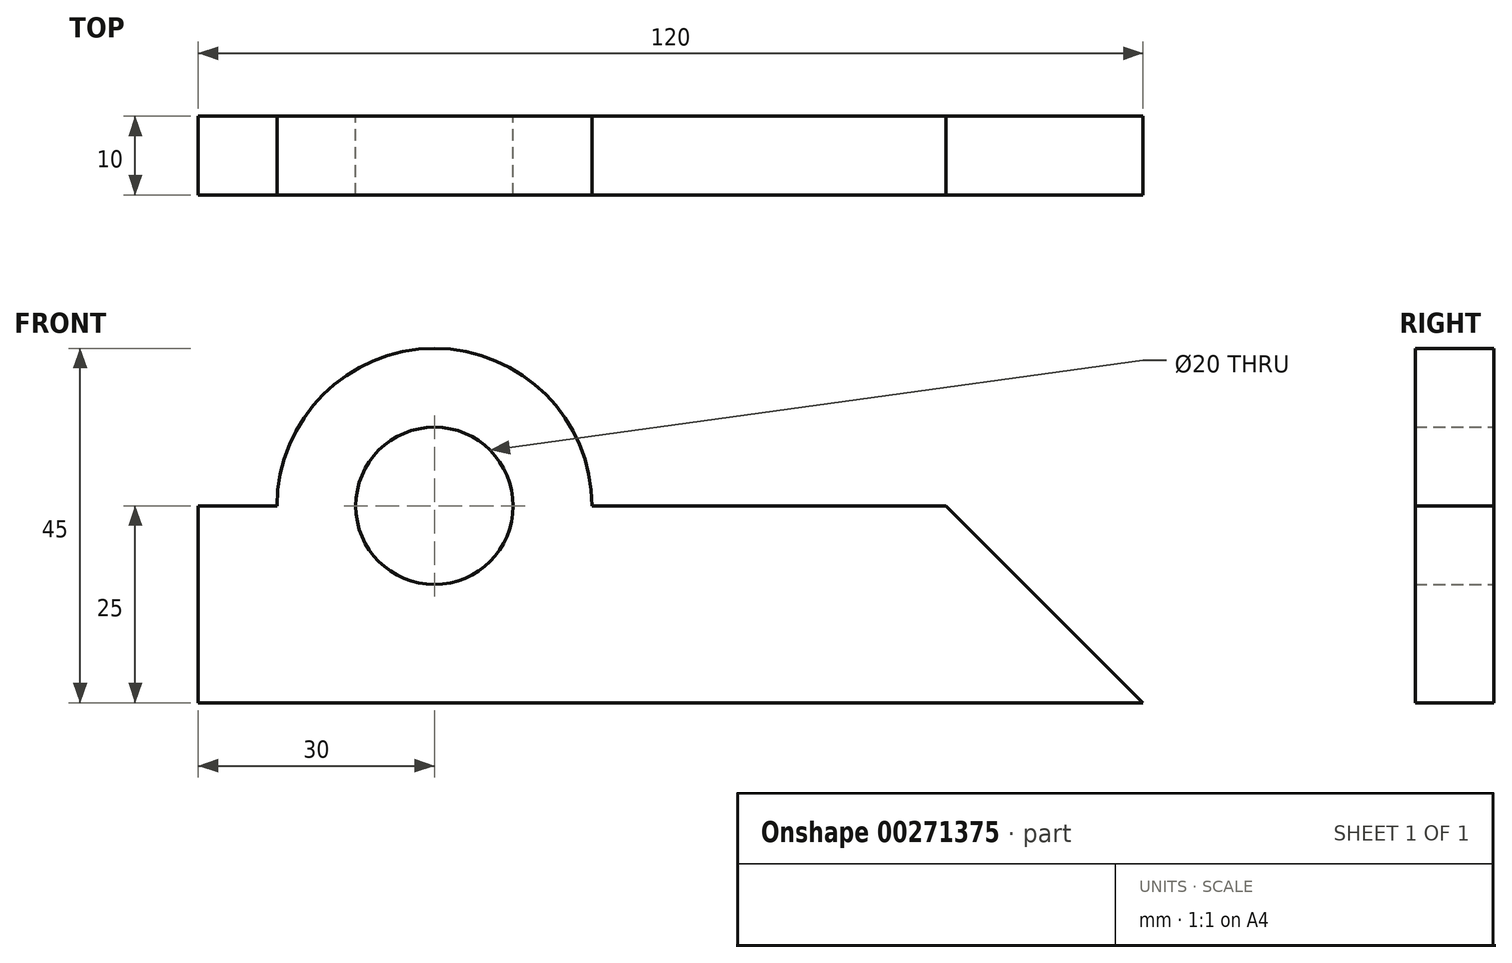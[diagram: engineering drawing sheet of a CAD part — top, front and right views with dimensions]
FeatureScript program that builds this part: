
annotation { "Feature Type Name" : "Feature", "Feature Type Description" : "" }
export const myFeature = defineFeature(function(context is Context, id is Id, definition is map)
    precondition{}
    {
        {
            var Q0;
            Q0=qCreatedBy(makeId("Front.planeOp"),FACE);
            var sketch = newSketch(context, id + "F0", { "sketchPlane" : qUnion([Q0])});
            skLineSegment(sketch, "E0", {"start": v(0, 0) * mm, "end": v(120, 0) * mm});
            skLineSegment(sketch, "E1", {"start": v(0, 0) * mm, "end": v(0, 25) * mm});
            skCircle(sketch, "E2", {"center": v(30, 25) * mm, "radius": 10 * mm});
            skLineSegment(sketch, "E3", {"start": v(0, 25) * mm, "end": v(10, 25) * mm});
            skLineSegment(sketch, "E4", {"start": v(120, 0) * mm, "end": v(95, 25) * mm});
            skLineSegment(sketch, "E5", {"start": v(95, 25) * mm, "end": v(50, 25) * mm});
            skArc(sketch, "E6", {"start": v(50, 25) * mm, "mid": v(30, 45) * mm, "end": v(10, 25) * mm});
            skSolve(sketch);
        }
        {
            var Q0;
            Q0=makeQuery(id+"F0.imprint","IMPRINT",FACE,{"disambiguationData":[TD([[makeQuery(id+"F0.imprint","IMPRINT",EDGE,{"derivedFrom":sQuery(id+"F0.wireOp",EDGE,"E0")}),1.0]])]});
            extrude(context, id + "F1", {"entities" : qUnion([Q0]), "depth" : 10 * mm});
        }
    });
